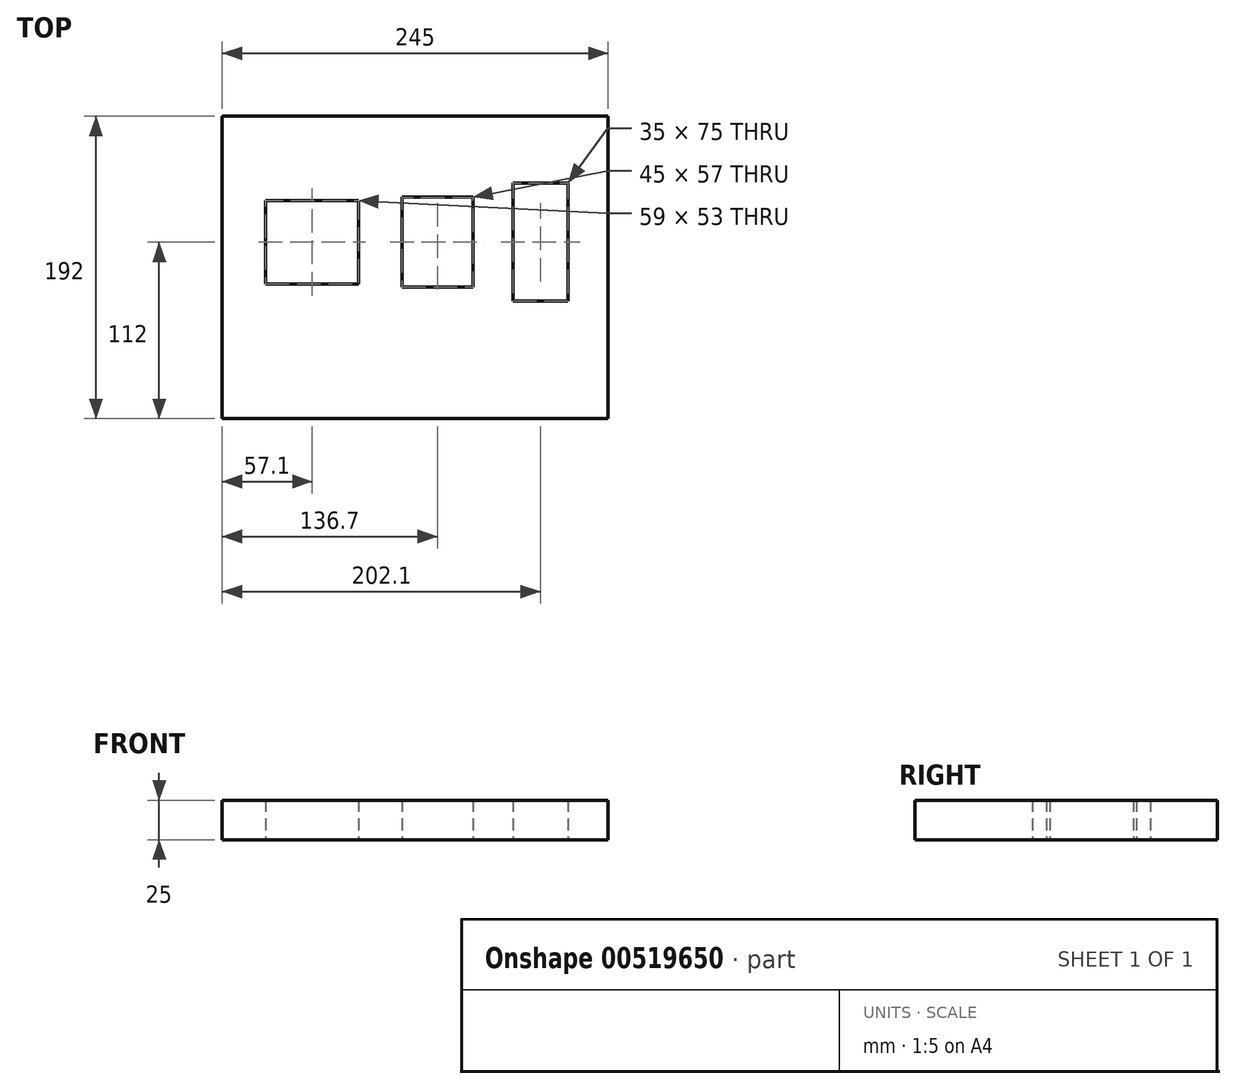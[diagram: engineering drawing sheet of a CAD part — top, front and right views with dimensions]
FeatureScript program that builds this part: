
annotation { "Feature Type Name" : "Feature", "Feature Type Description" : "" }
export const myFeature = defineFeature(function(context is Context, id is Id, definition is map)
    precondition{}
    {
        {
            var Q0;
            Q0=qCreatedBy(makeId("Top.planeOp"),FACE);
            var sketch = newSketch(context, id + "F0", { "sketchPlane" : qUnion([Q0])});
            skLineSegment(sketch, "E0.bottom", {"start": v(122.5, -112) * mm, "end": v(-122.5, -112) * mm});
            skLineSegment(sketch, "E0.top", {"start": v(122.5, 80) * mm, "end": v(-122.5, 80) * mm});
            skLineSegment(sketch, "E0.left", {"start": v(122.5, -112) * mm, "end": v(122.5, 80) * mm});
            skLineSegment(sketch, "E0.right", {"start": v(-122.5, -112) * mm, "end": v(-122.5, 80) * mm});
            skLineSegment(sketch, "E1", {"start": v(-122.5, -80) * mm, "end": v(122.5, -80) * mm});
            skLineSegment(sketch, "E2.bottom", {"start": v(-35.9, -26.5) * mm, "end": v(-94.9, -26.5) * mm});
            skLineSegment(sketch, "E2.top", {"start": v(-35.9, 26.5) * mm, "end": v(-94.9, 26.5) * mm});
            skLineSegment(sketch, "E2.left", {"start": v(-35.9, -26.5) * mm, "end": v(-35.9, 26.5) * mm});
            skLineSegment(sketch, "E2.right", {"start": v(-94.9, -26.5) * mm, "end": v(-94.9, 26.5) * mm});
            skPoint(sketch, "E2.middle", {"position": v(-65.4, 0) * mm});
            skLineSegment(sketch, "E3.bottom", {"start": v(36.7, -28.5) * mm, "end": v(-8.3, -28.5) * mm});
            skLineSegment(sketch, "E3.top", {"start": v(36.7, 28.5) * mm, "end": v(-8.3, 28.5) * mm});
            skLineSegment(sketch, "E3.left", {"start": v(36.7, -28.5) * mm, "end": v(36.7, 28.5) * mm});
            skLineSegment(sketch, "E3.right", {"start": v(-8.3, -28.5) * mm, "end": v(-8.3, 28.5) * mm});
            skPoint(sketch, "E3.middle", {"position": v(14.2, 0) * mm});
            skLineSegment(sketch, "E4.bottom", {"start": v(97.1, -37.5) * mm, "end": v(62.1, -37.5) * mm});
            skLineSegment(sketch, "E4.top", {"start": v(97.1, 37.5) * mm, "end": v(62.1, 37.5) * mm});
            skLineSegment(sketch, "E4.left", {"start": v(97.1, -37.5) * mm, "end": v(97.1, 37.5) * mm});
            skLineSegment(sketch, "E4.right", {"start": v(62.1, -37.5) * mm, "end": v(62.1, 37.5) * mm});
            skPoint(sketch, "E4.middle", {"position": v(79.6, 0) * mm});
            skPoint(sketch, "E5", {"position": v(0, 80) * mm});
            skSolve(sketch);
        }
        {
            var Q0;
            {var subQ0=sQuery(id+"F0.wireOp",EDGE,"E0.top");Q0=makeQuery(id+"F0.imprint","IMPRINT",FACE,{"disambiguationData":[TD([[makeQuery(id+"F0.imprint","IMPRINT",EDGE,{"derivedFrom":subQ0}),1.0]])]});}
            var Q1;
            {var subQ0=sQuery(id+"F0.wireOp",EDGE,"E0.bottom");Q1=makeQuery(id+"F0.imprint","IMPRINT",FACE,{"disambiguationData":[TD([[makeQuery(id+"F0.imprint","IMPRINT",EDGE,{"derivedFrom":subQ0}),-1.0]])]});}
            extrude(context, id + "F1", {"entities" : qUnion([Q0, Q1]), "depth" : 25 * mm, "offsetDistance" : 25 * mm});
        }
    });
